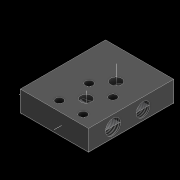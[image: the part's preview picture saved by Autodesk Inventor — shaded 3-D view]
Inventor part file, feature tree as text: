
AUTODESK INVENTOR PART (.ipt)
format: ipt  version: 2021 (Build 250183000, 183)  size: 283,648 bytes
history: native  units: in
note: dims shown in document units (in); Inventor stores cm internally (conversion verified against a paired STEP export)
features: other x12, direct_edit x5, hole x5, plane x4, move_body x4, sketch x3, extrude x2, thread x2, reference x2, mirror x1
ambient origin geometry x8: Origin, YZ Plane, XZ Plane, XY Plane, X Axis, Y Axis, Z Axis, Center Point
bodies: Solid1 (feature_tree)
feature tree (40):
  direct_edit  "Direct Edit1"
  plane  "Work Plane1"
  other  "Work Axis2"
  plane  "Work Plane2"
  extrude  "Extrusion1"  Depth=0.0591in TaperAngle=0.0deg
  plane  "Work Plane3"
  hole  "Hole2"  [1 undecoded]
  extrude  "Extrusion3"  Depth=1.9685in TaperAngle=0.0deg
  sketch  "Sketch4"  dims[d6=0.6184in d7=90.0deg d8=0.0in d9=0.0in d10=0.6299in]
  hole  "Hole6"  [1 undecoded]
  hole  "Hole7"  [1 undecoded]
  hole  "Hole10"  [1 undecoded]
  hole  "Hole12"  [1 undecoded]
  direct_edit  "Direct Edit4"
  direct_edit  "Direct Edit5"
  direct_edit  "Direct Edit6"
  direct_edit  "Direct Edit7"
  thread  "Thread1"  [1 undecoded]
  thread  "Thread3"  [1 undecoded]
  plane  "Work Plane4"
  mirror  "Mirror1"
  other  "Work Axis1"
  sketch  "Sketch3"  dims[d0=0.0in d1=0.0in d2=0.0591in d3=0.0in d4=0.0in d5=0.0591in]
  other  "Work Axis3"
  sketch  "Sketch6"  dims[d11=0.0in d12=0.0in d13=0.3937in d14=1.9685in d15=0.0in d16=0.315in d17=0.315in d20=0.2362in d28=0.2756in d29=0.2362in d30=0.1575in d31=0.0787in d32=90.0deg d33=1.9685in d34=0.8108in d35=0.4724in d36=1.3189in d37=0.0in d62=0.2362in d63=0.2362in d64=0.1575in d65=0.0787in d66=90.0deg d67=1.5123in d68=0.8108in d69=0.3937in d70=0.2362in d71=0.1575in d72=0.0787in d73=90.0deg d74=0.1575in d75=0.0in d90=0.315in d91=0.2362in d92=0.1575in d93=0.0787in d94=90.0deg d95=1.4961in d96=0.8108in d105=0.4331in d106=0.2362in d107=0.1575in d108=0.0787in d109=90.0deg d110=0.9449in d111=0.0in d112=-0.0394in d113=0.2362in d114=-0.0197in d115=-0.0394in d116=0.3937in d117=0.0in d120=0.3937in d121=0.0in d122=1.5748in d118=0.5635in d119=0.0295in d123=0.0148in]
  reference  "Reference1"
  reference  "Reference2"
  other  "Cut-Extrude26"
  move_body  "Move1"
  move_body  "Move2"
  move_body  "Move3"
  move_body  "Move4"
  parser-record x1  (decoder bookkeeping rows leaked as tree rows — omitted from the tree; the rows remain in map.json)
  other  "BodyV4.iam"
  other  "rotarynozzle:1"
  other  "iner_sleeve:1"
  other  "Size2"
  other  "Size3"
  other  "Size4"
  other  "Size5"
note: 7 required parameter values undecoded (feature->parameter linkage not recoverable at this tier; creation-order binding heuristic only, values carry confidence <= 0.55)
note: 1 file-system path scrubbed to <path> (originals preserved in map.json)
